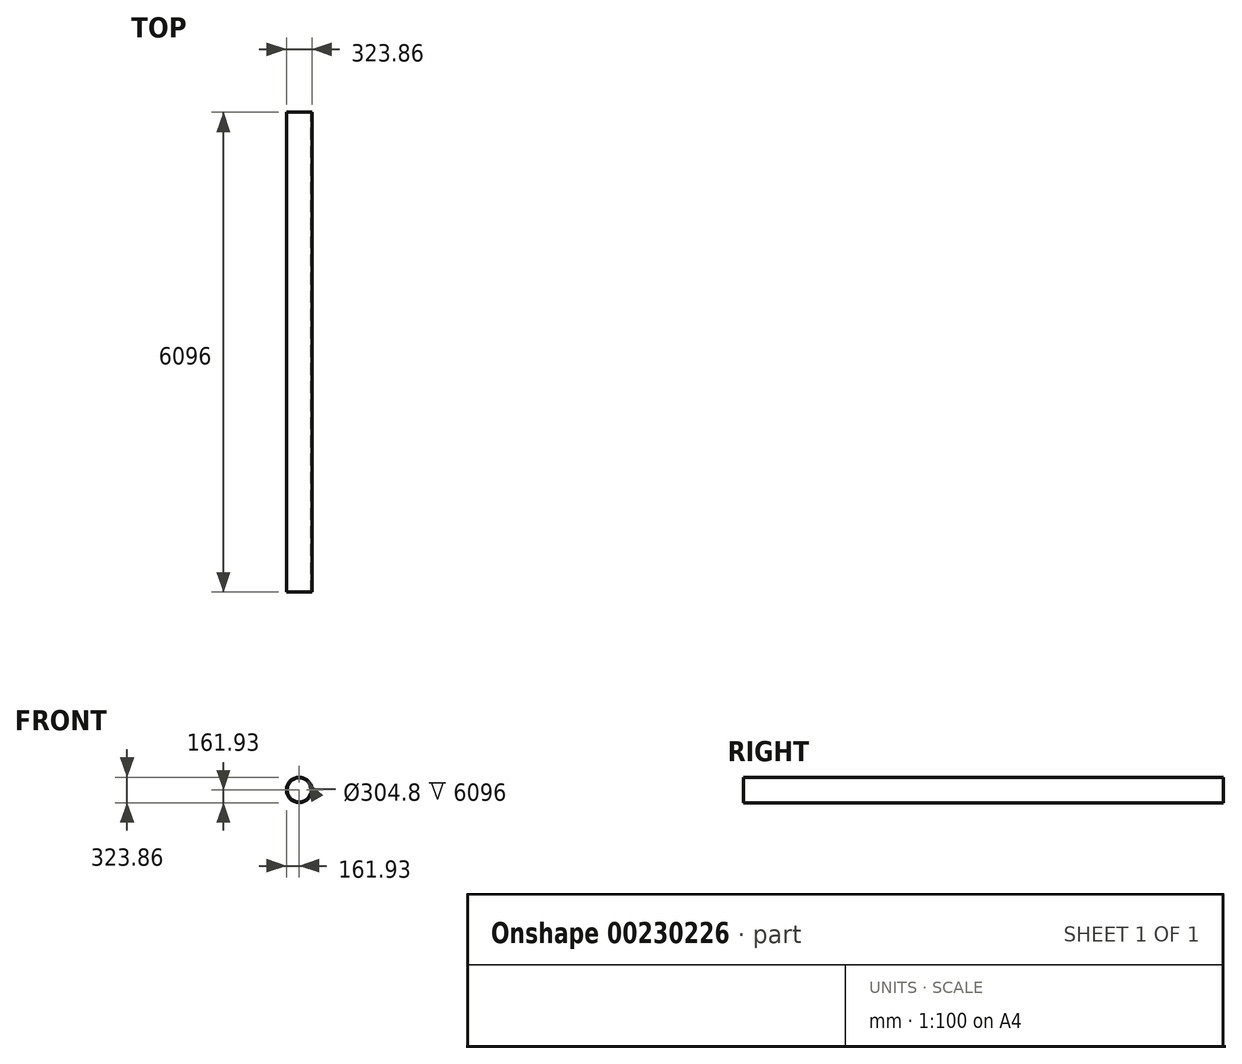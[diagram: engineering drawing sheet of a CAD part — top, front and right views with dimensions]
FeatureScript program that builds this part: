
annotation { "Feature Type Name" : "Feature", "Feature Type Description" : "" }
export const myFeature = defineFeature(function(context is Context, id is Id, definition is map)
    precondition{}
    {
        {
            var Q0;
            Q0=qCreatedBy(makeId("Front.planeOp"),FACE);
            var sketch = newSketch(context, id + "F0", { "sketchPlane" : qUnion([Q0])});
            skCircle(sketch, "E0", {"center": v(0, 0) * mm, "radius": 161.93 * mm});
            skCircle(sketch, "E1", {"center": v(0, 0) * mm, "radius": 152.4 * mm});
            skSolve(sketch);
        }
        {
            var Q0;
            Q0 = qSketchRegion(id + "F0", true);
            extrude(context, id + "F1", {"entities" : qUnion([Q0]), "depth" : 6096 * mm});
        }
    });
